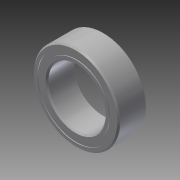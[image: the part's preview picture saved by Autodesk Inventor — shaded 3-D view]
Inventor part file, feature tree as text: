
AUTODESK INVENTOR PART (.ipt)
format: ipt  version: 2013 (Build 170138000, 138)  size: 532,480 bytes
history: native  units: in
note: dims shown in document units (in); Inventor stores cm internally (conversion verified against a paired STEP export)
features: imported_body x16, other x12, revolve x5
ambient origin geometry x8: Origin, YZ Plane, XZ Plane, XY Plane, X Axis, Y Axis, Z Axis, Center Point
feature tree (33):
  revolve  "Revolve1"  [1 undecoded]
  other  "217-2788_57155K3751"
  revolve  "Revolve3"  [1 undecoded]
  revolve  "Revolve4"  [1 undecoded]
  other  "CirPattern1[1]"
  other  "CirPattern1[2]"
  other  "CirPattern1[3]"
  other  "CirPattern1[4]"
  other  "CirPattern1[5]"
  other  "CirPattern1[6]"
  other  "CirPattern1[7]"
  other  "CirPattern1[8]"
  other  "CirPattern1[9]"
  other  "CirPattern1[10]"
  other  "CirPattern1[11]"
  revolve  "Revolve5[1]"  [1 undecoded]
  revolve  "Revolve5[2]"  [1 undecoded]
  imported_body  "Base1"
  imported_body  "Base2"
  imported_body  "Base3"
  imported_body  "Base4"
  imported_body  "Base5"
  imported_body  "Base6"
  imported_body  "Base7"
  imported_body  "Base8"
  imported_body  "Base9"
  imported_body  "Base10"
  imported_body  "Base11"
  imported_body  "Base12"
  imported_body  "Base13"
  imported_body  "Base14"
  imported_body  "Base15"
  imported_body  "Base16"
note: 5 required parameter values undecoded (feature->parameter linkage not recoverable at this tier; creation-order binding heuristic only, values carry confidence <= 0.55)
